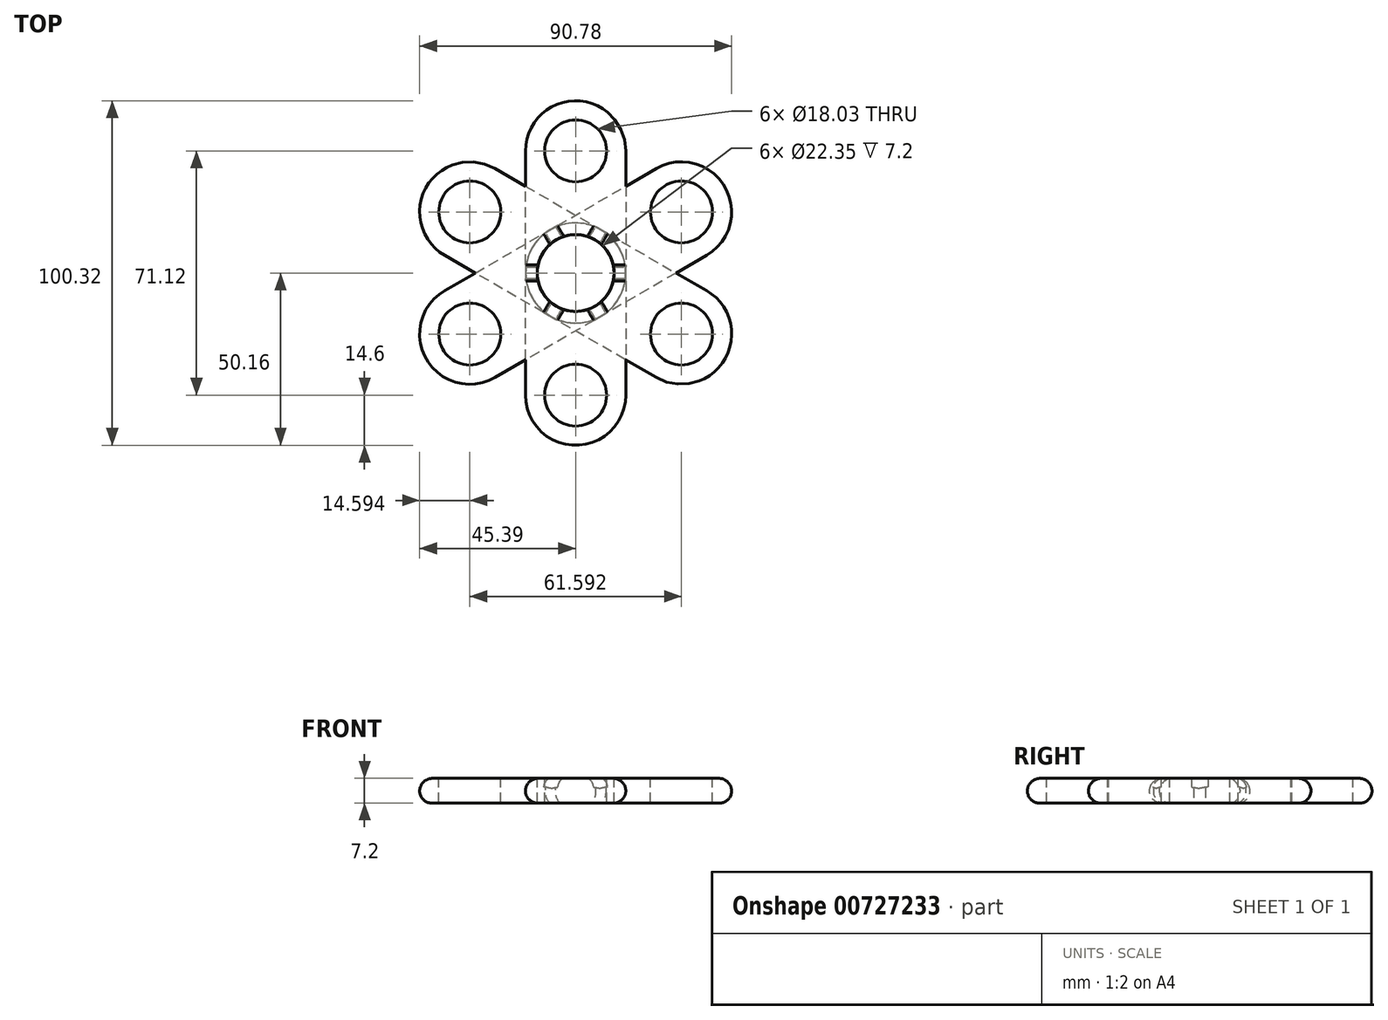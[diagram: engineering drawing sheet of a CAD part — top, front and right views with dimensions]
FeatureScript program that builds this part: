
annotation { "Feature Type Name" : "Feature", "Feature Type Description" : "" }
export const myFeature = defineFeature(function(context is Context, id is Id, definition is map)
    precondition{}
    {
        {
            var Q0;
            Q0=qCreatedBy(makeId("Top.planeOp"),FACE);
            var sketch = newSketch(context, id + "F0", { "sketchPlane" : qUnion([Q0])});
            skCircle(sketch, "E0", {"center": v(0, 0) * mm, "radius": 14.6 * mm});
            skLineSegment(sketch, "E1", {"start": v(-14.6, 0) * mm, "end": v(-14.6, -35.56) * mm});
            skLineSegment(sketch, "E2", {"start": v(14.6, 0) * mm, "end": v(14.6, -35.56) * mm});
            skCircle(sketch, "E3", {"center": v(0, -35.56) * mm, "radius": 14.6 * mm});
            skSolve(sketch);
        }
        {
            var Q0;
            Q0 = qSketchRegion(id + "F0", true);
            var Q1;
            Q1 = qSketchRegion(id + "F4", true);
            extrude(context, id + "F1", {"entities" : qUnion([Q0, Q1]), "depth" : 7.2 * mm, "offsetDistance" : 25.4 * mm});
        }
        {
            var Q0;
            Q0=makeQuery(id+"F1.opExtrude","CAP_FACE",FACE,{"disambiguationData":[OSD([sQuery(id+"F0.wireOp",EDGE,"E0"),sQuery(id+"F0.wireOp",EDGE,"E1"),sQuery(id+"F0.wireOp",EDGE,"E2"),sQuery(id+"F0.wireOp",EDGE,"E3")])],"isStart":false});
            var sketch = newSketch(context, id + "F2", { "sketchPlane" : qUnion([Q0])});
            skCircle(sketch, "E4", {"center": v(0, 0) * mm, "radius": 11.18 * mm});
            skLineSegment(sketch, "E5", {"start": v(0, 0) * mm, "end": v(0, -35.56) * mm});
            skCircle(sketch, "E6", {"center": v(0, -35.56) * mm, "radius": 9.02 * mm});
            skSolve(sketch);
        }
        {
            var Q0;
            Q0 = qSketchRegion(id + "F2", true);
            extrude(context, id + "F3", {"entities" : qUnion([Q0]), "operationType" : NewBodyOperationType.REMOVE, "endBound" : BoundingType.THROUGH_ALL, "oppositeDirection" : true, "depth" : 25.4 * mm, "offsetDistance" : 25.4 * mm});
        }
        {
            var Q0;
            Q0=qCreatedBy(makeId("Front.planeOp"),FACE);
            var sketch = newSketch(context, id + "F4", { "sketchPlane" : qUnion([Q0])});
            skLineSegment(sketch, "E7", {"start": v(0, 7.62) * mm, "end": v(0, 52.45) * mm});
            skSolve(sketch);
        }
        {
            var Q0;
            Q0=makeQuery(id+"F1.opExtrude","SWEPT_BODY",BODY,{"disambiguationData":[OSD([sQuery(id+"F0.wireOp",EDGE,"E0"),sQuery(id+"F0.wireOp",EDGE,"E1"),sQuery(id+"F0.wireOp",EDGE,"E2"),sQuery(id+"F0.wireOp",EDGE,"E3")])]});
            var Q1;
            Q1=sQuery(id+"F4.wireOp",EDGE,"E7");
            circularPattern(context, id + "F5", {"entities" : qUnion([Q0]), "axis" : qUnion([Q1]), "angle" : 360 * degree, "instanceCount" : 6, "oppositeDirection" : true, "equalSpace" : true});
        }
        {
            var Q0;
            Q0=makeQuery(id+"F5.opPattern","COPY",EDGE,{"derivedFrom":makeQuery(id+"F1.opExtrude","CAP_EDGE",EDGE,{"disambiguationData":[OSD([sQuery(id+"F0.wireOp",EDGE,"E3")])],"isStart":false}),"instanceName":"2"});
            var Q1;
            Q1=makeQuery(id+"F5.opPattern","COPY",EDGE,{"derivedFrom":makeQuery(id+"F1.opExtrude","CAP_EDGE",EDGE,{"disambiguationData":[OSD([sQuery(id+"F0.wireOp",EDGE,"E3")])],"isStart":false}),"instanceName":"1"});
            var Q2;
            Q2=makeQuery(id+"F1.opExtrude","CAP_EDGE",EDGE,{"disambiguationData":[OSD([sQuery(id+"F0.wireOp",EDGE,"E3")])],"isStart":false});
            var Q3;
            Q3=makeQuery(id+"F5.opPattern","COPY",EDGE,{"derivedFrom":makeQuery(id+"F1.opExtrude","CAP_EDGE",EDGE,{"disambiguationData":[OSD([sQuery(id+"F0.wireOp",EDGE,"E3")])],"isStart":false}),"instanceName":"5"});
            var Q4;
            Q4=makeQuery(id+"F5.opPattern","COPY",EDGE,{"derivedFrom":makeQuery(id+"F1.opExtrude","CAP_EDGE",EDGE,{"disambiguationData":[OSD([sQuery(id+"F0.wireOp",EDGE,"E3")])],"isStart":false}),"instanceName":"4"});
            var Q5;
            Q5=makeQuery(id+"F5.opPattern","COPY",EDGE,{"derivedFrom":makeQuery(id+"F1.opExtrude","CAP_EDGE",EDGE,{"disambiguationData":[OSD([sQuery(id+"F0.wireOp",EDGE,"E3")])],"isStart":false}),"instanceName":"3"});
            fillet(context, id + "F6", {"entities" : qUnion([Q0, Q1, Q2, Q3, Q4, Q5]), "radius" : 3.68 * mm, "tangentPropagation" : true, "allowEdgeOverflow" : false});
        }
        {
            var Q0;
            Q0=makeQuery(id+"F5.opPattern","COPY",EDGE,{"derivedFrom":makeQuery(id+"F1.opExtrude","CAP_EDGE",EDGE,{"disambiguationData":[OSD([sQuery(id+"F0.wireOp",EDGE,"E3")])],"isStart":true}),"instanceName":"3"});
            var Q1;
            Q1=makeQuery(id+"F5.opPattern","COPY",EDGE,{"derivedFrom":makeQuery(id+"F1.opExtrude","CAP_EDGE",EDGE,{"disambiguationData":[OSD([sQuery(id+"F0.wireOp",EDGE,"E3")])],"isStart":true}),"instanceName":"4"});
            var Q2;
            Q2=makeQuery(id+"F5.opPattern","COPY",EDGE,{"derivedFrom":makeQuery(id+"F1.opExtrude","CAP_EDGE",EDGE,{"disambiguationData":[OSD([sQuery(id+"F0.wireOp",EDGE,"E3")])],"isStart":true}),"instanceName":"5"});
            var Q3;
            Q3=makeQuery(id+"F1.opExtrude","CAP_EDGE",EDGE,{"disambiguationData":[OSD([sQuery(id+"F0.wireOp",EDGE,"E3")])],"isStart":true});
            var Q4;
            Q4=makeQuery(id+"F5.opPattern","COPY",EDGE,{"derivedFrom":makeQuery(id+"F1.opExtrude","CAP_EDGE",EDGE,{"disambiguationData":[OSD([sQuery(id+"F0.wireOp",EDGE,"E3")])],"isStart":true}),"instanceName":"1"});
            var Q5;
            Q5=makeQuery(id+"F5.opPattern","COPY",EDGE,{"derivedFrom":makeQuery(id+"F1.opExtrude","CAP_EDGE",EDGE,{"disambiguationData":[OSD([sQuery(id+"F0.wireOp",EDGE,"E3")])],"isStart":true}),"instanceName":"2"});
            fillet(context, id + "F7", {"entities" : qUnion([Q0, Q1, Q2, Q3, Q4, Q5]), "radius" : 3.56 * mm, "tangentPropagation" : true, "allowEdgeOverflow" : false});
        }
    });
